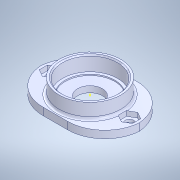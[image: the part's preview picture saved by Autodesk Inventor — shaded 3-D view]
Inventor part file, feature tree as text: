
AUTODESK INVENTOR PART (.ipt)
format: ipt  version: 2021 (Build 250183000, 183)  size: 208,896 bytes
history: mixed  units: in
note: dims shown in document units (in); Inventor stores cm internally (conversion verified against a paired STEP export)
features: sketch x7, extrude x5, delete_face x1, chamfer x1, fillet x1, other x1, imported_body x1
ambient origin geometry x8: Origin, YZ Plane, XZ Plane, XY Plane, X Axis, Y Axis, Z Axis, Center Point
bodies: Solid1 (imported_parasolid)
feature tree (17):
  extrude  "Extrusion1"  Depth=0.3937in TaperAngle=0.0deg
  extrude  "Extrusion2"  TaperAngle=0.0deg  [1 undecoded]
  sketch  "Sketch5"  dims[d8=0.9843in d9=0.3937in d10=0.0in]
  delete_face  "Delete Face1"
  extrude  "Extrusion4"  Depth=0.3937in TaperAngle=0.0deg
  extrude  "Extrusion5"  Depth=0.3937in TaperAngle=0.0deg
  chamfer  "Chamfer1"  Distance=0.0787in Angle=45.0deg
  sketch  "Sketch8"
  fillet  "Fillet1"  Radius=0.0394in
  extrude  "Extrusion8"  Depth=0.3937in TaperAngle=0.0deg
  sketch  "Sketch1"  dims[d0=0.7874in d1=0.3937in d2=0.0in]
  sketch  "Sketch2"  dims[d3=0.3937in d4=0.0in d5=0.0in]
  sketch  "Sketch6"  dims[d11=0.878in d12=0.3937in d13=0.0in d14=0.0197in d15=0.0787in d16=45.0deg d20=0.0394in]
  sketch  "Sketch7"  dims[d31=0.1378in d32=0.3937in d33=0.0in]
  sketch  "Sketch13"
  other  "Cut-Extrude3"
  imported_body  NMx_Import_Brep_tag  [imported B-rep: ~12 faces, bbox_mm=[32.0, 1.0, 0.0]]
note: 1 required parameter value undecoded (feature->parameter linkage not recoverable at this tier; creation-order binding heuristic only, values carry confidence <= 0.55)
